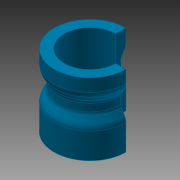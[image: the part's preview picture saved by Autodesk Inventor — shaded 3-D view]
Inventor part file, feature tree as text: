
AUTODESK INVENTOR PART (.ipt)
format: ipt  version: 2014 SP1 (Build 180222100, 222)  size: 139,264 bytes
history: native  units: in
note: dims shown in document units (in); Inventor stores cm internally (conversion verified against a paired STEP export)
features: revolve x1, fillet x1, sketch x1
ambient origin geometry x8: Origin, YZ Plane, XZ Plane, XY Plane, X Axis, Y Axis, Z Axis, Center Point
bodies: Solid1 (feature_tree)
feature tree (3):
  revolve  "Revolution1"  [1 undecoded]
  fillet  "Fillet1"  Radius=0.25in
  sketch  "Sketch1"  dims[d0=1.25in d1=0.5in d2=0.25in d3=150.0deg d4=0.75in d5=3.5in d6=150.0deg d7=0.5in d9=6.0in d10=270.0deg d11=0.5in d12=0.25in]
note: 1 required parameter value undecoded (feature->parameter linkage not recoverable at this tier; creation-order binding heuristic only, values carry confidence <= 0.55)
